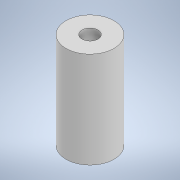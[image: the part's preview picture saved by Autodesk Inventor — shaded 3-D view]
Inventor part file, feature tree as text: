
AUTODESK INVENTOR PART (.ipt)
format: ipt  version: 2022 (Build 260153000, 153)  size: 97,280 bytes
history: native  units: in
note: dims shown in document units (in); Inventor stores cm internally (conversion verified against a paired STEP export)
features: extrude x2, sketch x2
ambient origin geometry x8: Origin, YZ Plane, XZ Plane, XY Plane, X Axis, Y Axis, Z Axis, Center Point
bodies: Solid1 (feature_tree)
feature tree (4):
  extrude  "Extrusion1"  Depth=1.1811in TaperAngle=0.0deg
  extrude  "Extrusion2"  Depth=1.5748in TaperAngle=0.0deg
  sketch  "Sketch1"  dims[d0=0.5906in d1=1.1811in d2=0.0in]
  sketch  "Sketch2"  dims[d3=0.1969in d4=1.5748in d5=0.0in]
